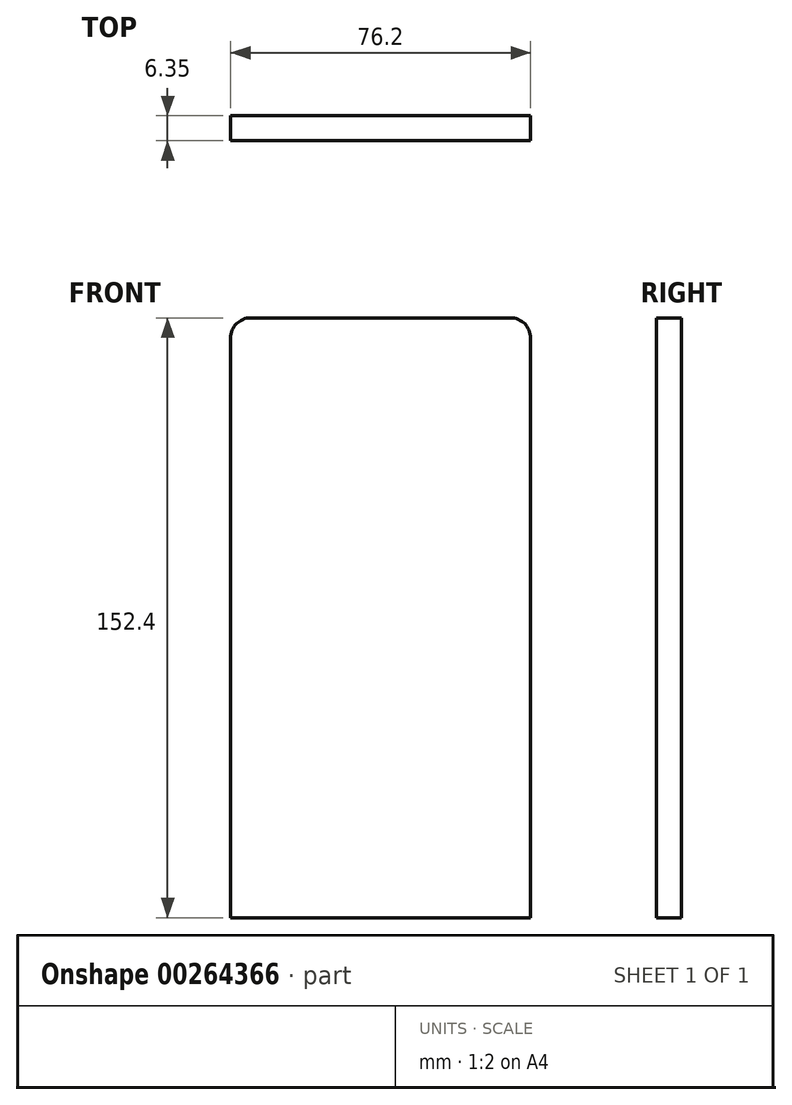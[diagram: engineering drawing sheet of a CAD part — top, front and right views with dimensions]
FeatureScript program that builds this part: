
annotation { "Feature Type Name" : "Feature", "Feature Type Description" : "" }
export const myFeature = defineFeature(function(context is Context, id is Id, definition is map)
    precondition{}
    {
        {
            var Q0;
            Q0=qCreatedBy(makeId("Front.planeOp"),FACE);
            var sketch = newSketch(context, id + "F0", { "sketchPlane" : qUnion([Q0])});
            skLineSegment(sketch, "E0.bottom", {"start": v(38.1, 76.2) * mm, "end": v(-38.1, 76.2) * mm});
            skLineSegment(sketch, "E0.top", {"start": v(38.1, -76.2) * mm, "end": v(-38.1, -76.2) * mm});
            skLineSegment(sketch, "E0.left", {"start": v(38.1, 76.2) * mm, "end": v(38.1, -76.2) * mm});
            skLineSegment(sketch, "E0.right", {"start": v(-38.1, 76.2) * mm, "end": v(-38.1, -76.2) * mm});
            skPoint(sketch, "E0.middle", {"position": v(0, 0) * mm});
            skSolve(sketch);
        }
        {
            var Q0;
            Q0=makeQuery(id+"F0.imprint","IMPRINT",FACE,{"disambiguationData":[TD([[makeQuery(id+"F0.imprint","IMPRINT",EDGE,{"derivedFrom":sQuery(id+"F0.wireOp",EDGE,"E0.bottom")}),1.0]])]});
            extrude(context, id + "F1", {"entities" : qUnion([Q0]), "depth" : 6.35 * mm});
        }
        {
            var Q0;
            Q0=makeQuery(id+"F1.opExtrude","SWEPT_EDGE",EDGE,{"disambiguationData":[OSD([sQuery(id+"F0.wireOp",EDGE,"E0.bottom"),sQuery(id+"F0.wireOp",EDGE,"E0.right")])]});
            fillet(context, id + "F2", {"entities" : qUnion([Q0]), "radius" : 5.08 * mm, "tangentPropagation" : true, "allowEdgeOverflow" : false});
        }
        {
            var Q0;
            Q0=makeQuery(id+"F1.opExtrude","SWEPT_EDGE",EDGE,{"disambiguationData":[OSD([sQuery(id+"F0.wireOp",EDGE,"E0.bottom"),sQuery(id+"F0.wireOp",EDGE,"E0.left")])]});
            fillet(context, id + "F3", {"entities" : qUnion([Q0]), "radius" : 5.08 * mm, "tangentPropagation" : true, "allowEdgeOverflow" : false});
        }
    });
